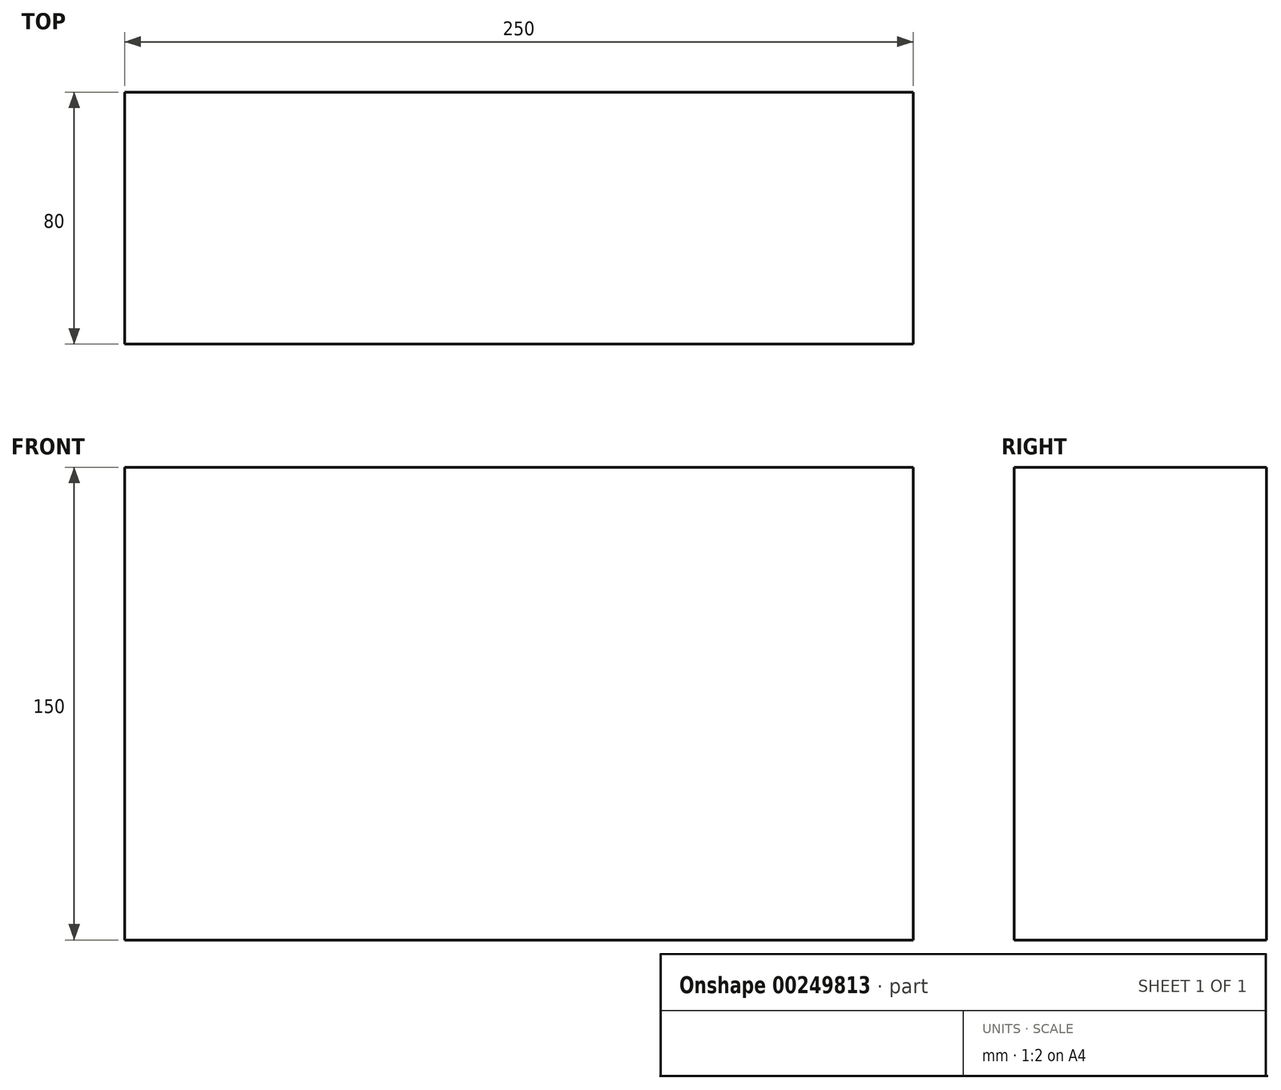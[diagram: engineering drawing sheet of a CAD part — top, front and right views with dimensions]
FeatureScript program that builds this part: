
annotation { "Feature Type Name" : "Feature", "Feature Type Description" : "" }
export const myFeature = defineFeature(function(context is Context, id is Id, definition is map)
    precondition{}
    {
        {
            var Q0;
            Q0=qCreatedBy(makeId("Front.planeOp"),FACE);
            var sketch = newSketch(context, id + "F0", { "sketchPlane" : qUnion([Q0])});
            skLineSegment(sketch, "E0.bottom", {"start": v(0, 0) * mm, "end": v(250, 0) * mm});
            skLineSegment(sketch, "E0.top", {"start": v(0, 150) * mm, "end": v(250, 150) * mm});
            skLineSegment(sketch, "E0.left", {"start": v(0, 0) * mm, "end": v(0, 150) * mm});
            skLineSegment(sketch, "E0.right", {"start": v(250, 0) * mm, "end": v(250, 150) * mm});
            skSolve(sketch);
        }
        {
            var Q0;
            Q0 = qSketchRegion(id + "F0", true);
            extrude(context, id + "F1", {"entities" : qUnion([Q0]), "depth" : 80 * mm});
        }
    });
